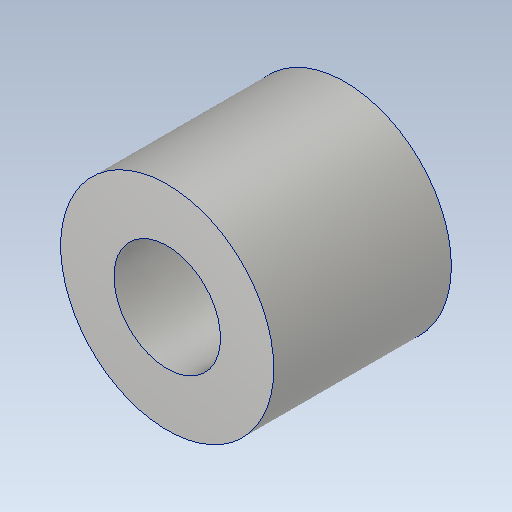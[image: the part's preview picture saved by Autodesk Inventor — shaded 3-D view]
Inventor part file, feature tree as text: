
AUTODESK INVENTOR PART (.ipt)
format: ipt  version: 2020.2 (Build 242310000, 310)  size: 119,808 bytes
history: native  units: mm
features: other x1, extrude x1, sketch x1
ambient origin geometry x8: Origin, YZ Plane, XZ Plane, XY Plane, X Axis, Y Axis, Z Axis, Center Point
bodies: Body1 (feature_tree)
feature tree (3):
  other  "ソリッド1"
  extrude  "押し出し1"  Depth=6.0mm
  sketch  "スケッチ1"
